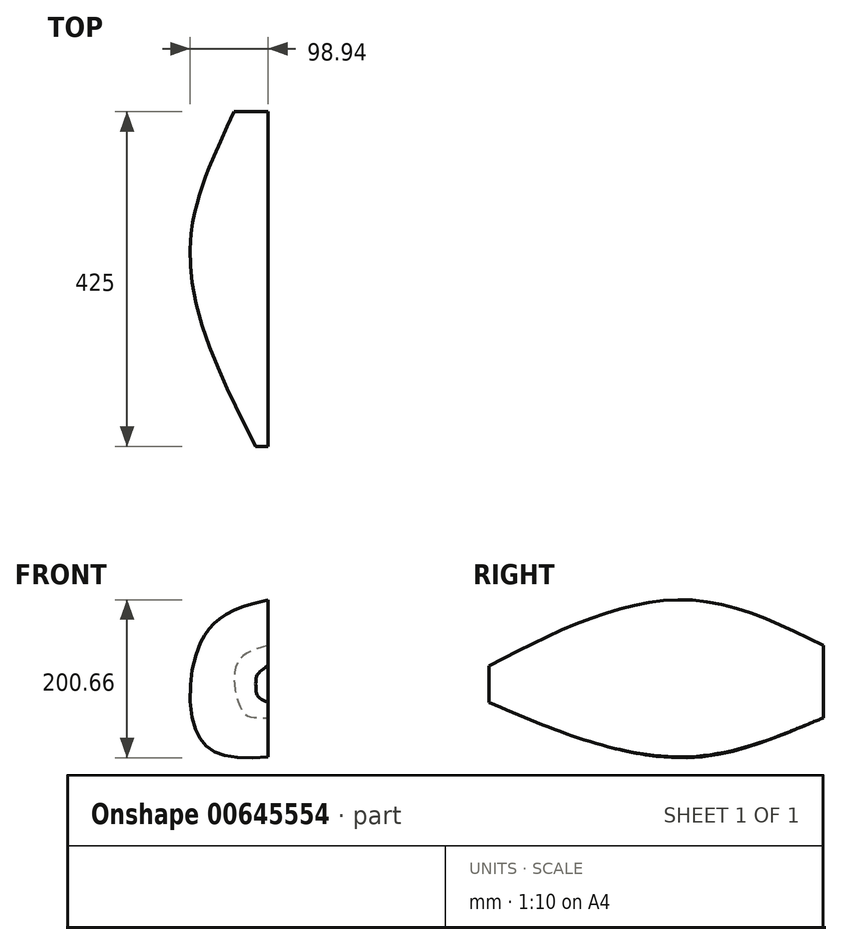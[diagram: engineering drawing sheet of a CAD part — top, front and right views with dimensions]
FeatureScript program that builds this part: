
annotation { "Feature Type Name" : "Feature", "Feature Type Description" : "" }
export const myFeature = defineFeature(function(context is Context, id is Id, definition is map)
    precondition{}
    {
        {
            var Q0;
            Q0=qCreatedBy(makeId("Front.planeOp"),FACE);
            cPlane(context, id + "F0", {"entities" : qUnion([Q0]), "cplaneType" : CPlaneType.OFFSET, "offset" : 150 * mm, "width" : 150 * mm, "height" : 150 * mm});
        }
        {
            var Q0;
            Q0=qCreatedBy(id+"F0.planeOp",FACE);
            cPlane(context, id + "F1", {"entities" : qUnion([Q0]), "cplaneType" : CPlaneType.OFFSET, "offset" : 275 * mm, "width" : 150 * mm, "height" : 150 * mm});
        }
        {
            var Q0;
            Q0=qCreatedBy(makeId("Front.planeOp"),FACE);
            var sketch = newSketch(context, id + "F2", { "sketchPlane" : qUnion([Q0])});
            skLineSegment(sketch, "E0", {"start": v(0, -44.83) * mm, "end": v(0, 46.8) * mm});
            skFitSpline(sketch, "E1", {"points": [v(0, 46.8) * mm, v(-41.05, 19.26) * mm, v(-30.36, -38.65) * mm, v(0, -44.83) * mm], "startDerivative": vector(-189.7, -48.62) * mm, "endDerivative": vector(161.15, -7.6) * mm});
            skSolve(sketch);
        }
        {
            var Q0;
            Q0=qCreatedBy(id+"F0.planeOp",FACE);
            var sketch = newSketch(context, id + "F3", { "sketchPlane" : qUnion([Q0])});
            skLineSegment(sketch, "E2", {"start": v(0, 102.95) * mm, "end": v(0, -92.62) * mm});
            skFitSpline(sketch, "E3", {"points": [v(0, 102.95) * mm, v(-81.35, 55.32) * mm, v(-77.57, -78.46) * mm, v(0, -92.62) * mm], "startDerivative": vector(-308.29, -70.8) * mm, "endDerivative": vector(217.17, 9.9) * mm});
            skSolve(sketch);
        }
        {
            var Q0;
            Q0=qCreatedBy(id+"F1.planeOp",FACE);
            var sketch = newSketch(context, id + "F4", { "sketchPlane" : qUnion([Q0])});
            skLineSegment(sketch, "E4", {"start": v(0, -25.4) * mm, "end": v(0, 21.26) * mm});
            skFitSpline(sketch, "E5", {"points": [v(0, 21.26) * mm, v(-14.02, 8.33) * mm, v(-15.15, -8.54) * mm, v(0, -25.4) * mm], "startDerivative": vector(-74.9, -59.08) * mm, "endDerivative": vector(116.11, -46.55) * mm});
            skSolve(sketch);
        }
        {
            var Q0;
            Q0=makeQuery(id+"F2.imprint","IMPRINT",FACE,{"disambiguationData":[TD([[makeQuery(id+"F2.imprint","IMPRINT",EDGE,{"derivedFrom":sQuery(id+"F2.wireOp",EDGE,"E0")}),1.0]])]});
            var Q1;
            Q1=makeQuery(id+"F3.imprint","IMPRINT",FACE,{"disambiguationData":[TD([[makeQuery(id+"F3.imprint","IMPRINT",EDGE,{"derivedFrom":sQuery(id+"F3.wireOp",EDGE,"E2")}),-1.0]])]});
            var Q2;
            Q2=makeQuery(id+"F4.imprint","IMPRINT",FACE,{"disambiguationData":[TD([[makeQuery(id+"F4.imprint","IMPRINT",EDGE,{"derivedFrom":sQuery(id+"F4.wireOp",EDGE,"E4")}),1.0]])]});
            loft(context, id + "F5", {"sheetProfilesArray" : [{ "sheetProfileEntities" : qUnion([Q0]) }, { "sheetProfileEntities" : qUnion([Q1]) }, { "sheetProfileEntities" : qUnion([Q2]) }]});
        }
    });
